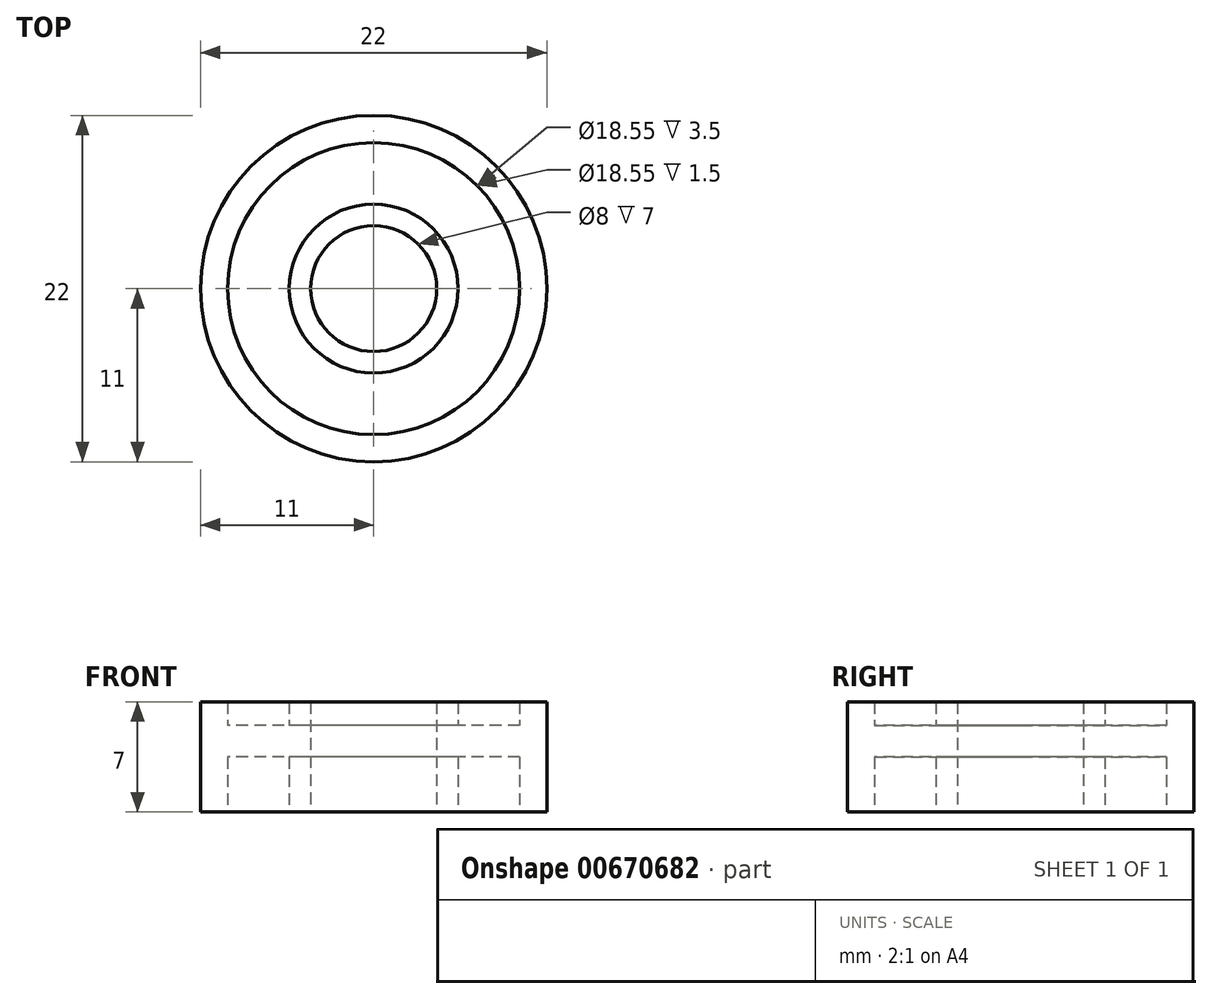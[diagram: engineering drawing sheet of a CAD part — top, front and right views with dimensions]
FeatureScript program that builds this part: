
annotation { "Feature Type Name" : "Feature", "Feature Type Description" : "" }
export const myFeature = defineFeature(function(context is Context, id is Id, definition is map)
    precondition{}
    {
        {
            var Q0;
            Q0=qCreatedBy(makeId("Top.planeOp"),FACE);
            var sketch = newSketch(context, id + "F0", { "sketchPlane" : qUnion([Q0])});
            skCircle(sketch, "E0", {"center": v(0, 0) * mm, "radius": 11 * mm});
            skCircle(sketch, "E1", {"center": v(0, 0) * mm, "radius": 9.27 * mm});
            skCircle(sketch, "E2", {"center": v(0, 0) * mm, "radius": 5.36 * mm});
            skCircle(sketch, "E3", {"center": v(0, 0) * mm, "radius": 4 * mm});
            skSolve(sketch);
        }
        {
            var Q0;
            Q0=makeQuery(id+"F0.imprint","IMPRINT",FACE,{"disambiguationData":[TD([[makeQuery(id+"F0.imprint","IMPRINT",EDGE,{"derivedFrom":sQuery(id+"F0.wireOp",EDGE,"E0")}),1.0]])]});
            var Q1;
            Q1=makeQuery(id+"F0.imprint","IMPRINT",FACE,{"disambiguationData":[TD([[makeQuery(id+"F0.imprint","IMPRINT",EDGE,{"derivedFrom":sQuery(id+"F0.wireOp",EDGE,"E2")}),1.0]])]});
            extrude(context, id + "F1", {"entities" : qUnion([Q0, Q1]), "endBound" : BoundingType.SYMMETRIC, "depth" : 7 * mm, "offsetDistance" : 25 * mm});
        }
        {
            var Q0;
            Q0=makeQuery(id+"F0.imprint","IMPRINT",FACE,{"disambiguationData":[TD([[makeQuery(id+"F0.imprint","IMPRINT",EDGE,{"derivedFrom":sQuery(id+"F0.wireOp",EDGE,"E1")}),1.0]])]});
            extrude(context, id + "F2", {"entities" : qUnion([Q0]), "operationType" : NewBodyOperationType.ADD, "depth" : 2 * mm, "offsetDistance" : 25 * mm});
        }
    });
